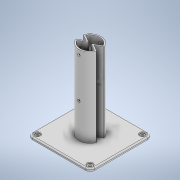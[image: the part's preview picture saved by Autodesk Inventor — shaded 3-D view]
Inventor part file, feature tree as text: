
AUTODESK INVENTOR PART (.ipt)
format: ipt  version: 2020 (Build 240168000, 168)  size: 224,256 bytes
history: native  units: in
note: dims shown in document units (in); Inventor stores cm internally (conversion verified against a paired STEP export)
features: extrude x7, sketch x7, mirror x2, fillet x2, shell x1, projected_geometry x1
ambient origin geometry x8: Origin, YZ Plane, XZ Plane, XY Plane, X Axis, Y Axis, Z Axis, Center Point
bodies: Solid1 (feature_tree)
feature tree (20):
  extrude  "Extrusion1"  Depth=0.2in
  shell  "Shell1"  Thickness=30.0deg
  extrude  "Extrusion2"  Depth=4.0in
  extrude  "Extrusion3"  Depth=3.1496in
  extrude  "Extrusion4"  Depth=0.125in TaperAngle=0.0deg
  extrude  "Extrusion5"  Depth=0.125in
  extrude  "Extrusion6"  Depth=4.0in TaperAngle=0.0deg
  extrude  "Extrusion7"  Depth=0.025in
  mirror  "Mirror1"
  mirror  "Mirror2"
  fillet  "Fillet1"  Radius=4.0in
  fillet  "Fillet2"  Radius=0.1339in
  sketch  "Sketch1"  dims[d0=1.125in d1=0.2in d2=30.0deg]
  sketch  "Sketch2"  dims[d3=4.0in d4=0.0in d5=0.0669in]
  sketch  "Sketch3"  dims[d6=3.1496in d7=3.1496in]
  projected_geometry  "Projected Loop1"
  sketch  "Sketch4"  dims[d9=0.25in d10=0.125in d11=0.0in]
  sketch  "Sketch5"  dims[d12=0.0669in d13=0.0in d14=0.125in]
  sketch  "Sketch6"  dims[d15=1.75in d16=4.0in d17=0.0in]
  sketch  "Sketch7"  dims[d18=0.125in d19=3.75in d20=4.0in d21=2.0in d22=0.0in d23=0.0in d24=0.1339in d25=1.0in d26=0.0in d27=0.25in d28=0.05in d29=0.0in d30=0.0625in d31=0.025in]
